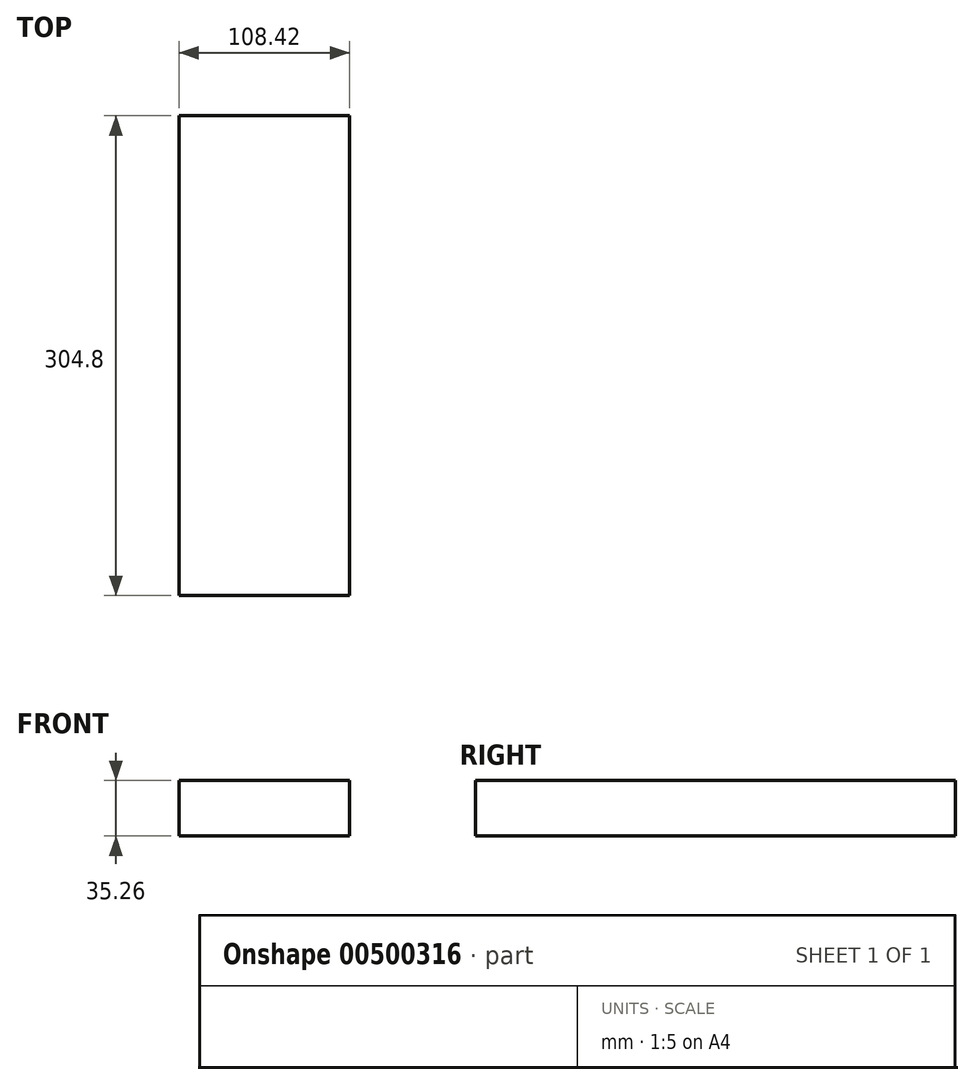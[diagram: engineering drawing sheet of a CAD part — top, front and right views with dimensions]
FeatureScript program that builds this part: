
annotation { "Feature Type Name" : "Feature", "Feature Type Description" : "" }
export const myFeature = defineFeature(function(context is Context, id is Id, definition is map)
    precondition{}
    {
        {
            var Q0;
            Q0=qCreatedBy(makeId("Front.planeOp"),FACE);
            var sketch = newSketch(context, id + "F0", { "sketchPlane" : qUnion([Q0])});
            skLineSegment(sketch, "E0.bottom", {"start": v(-54.21, 17.63) * mm, "end": v(54.21, 17.63) * mm});
            skLineSegment(sketch, "E0.top", {"start": v(-54.21, -17.63) * mm, "end": v(54.21, -17.63) * mm});
            skLineSegment(sketch, "E0.left", {"start": v(-54.21, 17.63) * mm, "end": v(-54.21, -17.63) * mm});
            skLineSegment(sketch, "E0.right", {"start": v(54.21, 17.63) * mm, "end": v(54.21, -17.63) * mm});
            skPoint(sketch, "E0.middle", {"position": v(0, 0) * mm});
            skSolve(sketch);
        }
        {
            var Q0;
            Q0=makeQuery(id+"F0.imprint","IMPRINT",FACE,{"disambiguationData":[TD([[makeQuery(id+"F0.imprint","IMPRINT",EDGE,{"derivedFrom":sQuery(id+"F0.wireOp",EDGE,"E0.bottom")}),-1.0]])]});
            extrude(context, id + "F1", {"entities" : qUnion([Q0]), "depth" : 304.8 * mm});
        }
    });
